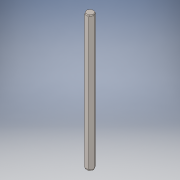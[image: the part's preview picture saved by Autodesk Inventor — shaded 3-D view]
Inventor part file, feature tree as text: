
AUTODESK INVENTOR PART (.ipt)
format: ipt  version: 2019.1 (Build 231200000, 200)  size: 125,952 bytes
history: mixed  units: in
note: dims shown in document units (in); Inventor stores cm internally (conversion verified against a paired STEP export)
features: fillet x1, imported_body x1
ambient origin geometry x8: Origin, YZ Plane, XZ Plane, XY Plane, X Axis, Y Axis, Z Axis, Center Point
bodies: Solid1 (imported_parasolid)
feature tree (2):
  fillet  "Fillet1"  [1 undecoded]
  imported_body  NMx_Import_Brep_tag  [imported B-rep: ~32 faces, bbox_mm=[3.0, 50.0, 2.598076]]
note: 1 required parameter value undecoded (feature->parameter linkage not recoverable at this tier; creation-order binding heuristic only, values carry confidence <= 0.55)
